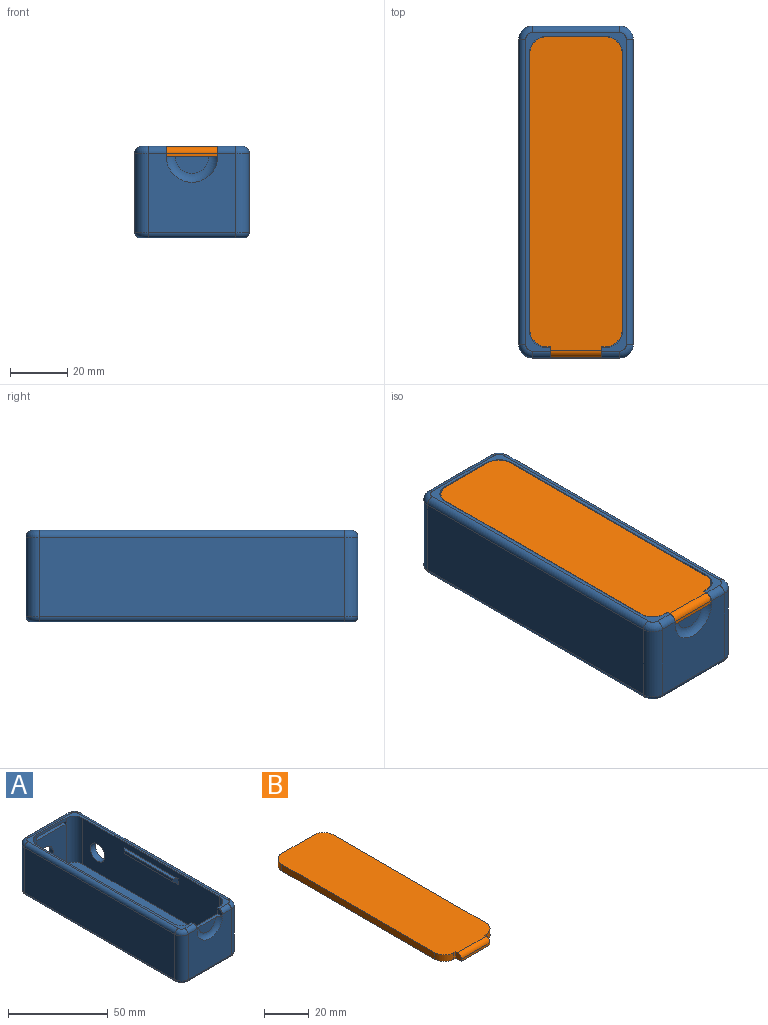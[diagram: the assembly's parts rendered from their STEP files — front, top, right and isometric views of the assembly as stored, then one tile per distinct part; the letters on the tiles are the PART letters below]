
ASSEMBLY  parts=2 mates=1
PART A: 69 faces, bbox 40.8x118.2x32 mm
  f0: plane 96.81x28.4mm, normal (1,0,0), area 2611.4mm2, adj f4,f11,f16,f17,f52,f57,f58,f59
  f1: plane 96.81x28.4mm, normal (-1,0,0), area 2524.9mm2, adj f4,f11,f18,f19,f21,f50,f54,f55
  f2: plane 30.66x27.84mm, normal (0,1,0), area 403.1mm2, adj f12,f13,f34,f44,f47
  f3: plane 20.8x1.7mm, normal (0,-1,0), area 35.4mm2, adj f4,f17,f18,f28
  f4: plane 111.25x35.25mm, normal (0,0,1), area 356.9mm2, adj f0,f1,f3,f5,f16,f17,f18,f19
  f5: plane 28.4x20.8mm, normal (0,1,0), area 526.1mm2, adj f4,f11,f16,f19,f22,f23,f24
  f6: plane 30.64x27.82mm, normal (0,-1,0), area 703.3mm2, adj f14,f15,f22,f24,f30,f38,f41,f61
  f7: plane 24.72x21.87mm, normal (0,-1,0), area 432.7mm2, adj f11,f17,f18,f20,f26,f66
  f8: plane 106.64x27.82mm, normal (1,0,0), area 2880.6mm2, adj f12,f15,f21,f32,f45
  f9: plane 106.64x27.82mm, normal (-1,0,0), area 2967.2mm2, adj f13,f14,f36,f40
  f10: plane 112.4x36.4mm, normal (0,0,-1), area 4084.2mm2, adj f39,f40,f41,f42,f43,f44,f45,f46
  f11: plane 108.8x32.8mm, normal (0,0,1), area 3460.8mm2, adj f0,f1,f5,f7,f16,f17,f18,f19
  f12: cylinder r=4.68mm len=27.82mm, axis (0,0,-1), area 204.5mm2, adj f2,f8,f33,f46
  f13: cylinder r=4.68mm len=27.82mm, axis (0,0,1), area 201.6mm2, adj f2,f9,f35,f42,f47
  f14: cylinder r=4.68mm len=27.82mm, axis (0,0,-1), area 204.5mm2, adj f6,f9,f37,f39
  f15: cylinder r=4.68mm len=27.82mm, axis (0,0,1), area 204.5mm2, adj f6,f8,f31,f43
  f16: cylinder r=6mm len=28.4mm, axis (0,0,1), area 267.6mm2, adj f0,f4,f5,f11
  f17: cylinder r=6mm len=28.4mm, axis (0,0,-1), area 262.1mm2, adj f0,f3,f4,f7,f11,f25,f66
  f18: cylinder r=6mm len=28.4mm, axis (0,0,1), area 267.6mm2, adj f1,f3,f4,f7,f11,f27
  f19: cylinder r=6mm len=28.4mm, axis (0,0,-1), area 267.6mm2, adj f1,f4,f5,f11
  f20: cylinder r=5.25mm len=10.5mm, axis (0,1,0), area 85.8mm2, adj f7,f48
  f21: cylinder r=5.25mm len=10.5mm, axis (1,0,0), area 118.8mm2, adj f1,f8
  f22: plane 3.6x3.6mm, normal (1,0,0), area 11.7mm2, adj f4,f5,f6,f23,f38
  f23: plane 18x3.6mm, normal (0,0,1), area 35.7mm2, adj f5,f22,f24,f60,f61
  f24: plane 3.6x3.6mm, normal (-1,0,0), area 11.7mm2, adj f4,f5,f6,f23,f30
  f25: plane 2.1x2mm, normal (1,0,0), area 4.1mm2, adj f17,f26,f28,f29,f49
  f26: plane 20.8x2.1mm, normal (0,0,1), area 43.7mm2, adj f7,f25,f27,f29
  f27: plane 2.1x2mm, normal (-1,0,0), area 4.1mm2, adj f18,f26,f28,f29,f49
  f28: plane 20.8x1.6mm, normal (0,0,-1), area 33.3mm2, adj f3,f25,f27,f49
  f29: plane 20.8x1.5mm, normal (0,-1,0), area 31.2mm2, adj f25,f26,f27,f49
  f30: cylinder r=2.38mm len=6.32mm, axis (-1,0,0), area 23.6mm2, adj f4,f6,f24,f31
  f31: torus R=2.3mm, axis (0,0,1), area 22.4mm2, adj f4,f15,f30,f32
  f32: cylinder r=2.38mm len=106.64mm, axis (0,-1,0), area 398mm2, adj f4,f8,f31,f33
  f33: torus R=2.3mm, axis (0,0,1), area 22.4mm2, adj f4,f12,f32,f34
  f34: cylinder r=2.38mm len=30.64mm, axis (1,0,0), area 114.4mm2, adj f2,f4,f33,f35
  f35: torus R=2.3mm, axis (0,0,1), area 22.4mm2, adj f4,f13,f34,f36
  f36: cylinder r=2.38mm len=106.64mm, axis (0,1,0), area 398mm2, adj f4,f9,f35,f37
  f37: torus R=2.3mm, axis (0,0,1), area 22.4mm2, adj f4,f14,f36,f38
  f38: cylinder r=2.38mm len=6.32mm, axis (-1,0,0), area 23.6mm2, adj f4,f6,f22,f37
  f39: torus R=2.88mm, axis (0,0,1), area 17.9mm2, adj f10,f14,f40,f41
  f40: cylinder r=1.8mm len=106.64mm, axis (0,-1,0), area 301.5mm2, adj f9,f10,f39,f42
  f41: cylinder r=1.8mm len=30.64mm, axis (1,0,0), area 86.6mm2, adj f6,f10,f39,f43
  f42: torus R=2.88mm, axis (0,0,1), area 17.9mm2, adj f10,f13,f40,f44
  f43: torus R=2.88mm, axis (0,0,1), area 17.9mm2, adj f10,f15,f41,f45
  f44: cylinder r=1.8mm len=30.64mm, axis (-1,0,0), area 86.6mm2, adj f2,f10,f42,f46
  f45: cylinder r=1.8mm len=106.64mm, axis (0,1,0), area 301.5mm2, adj f8,f10,f43,f46
  f46: torus R=2.88mm, axis (0,0,1), area 17.9mm2, adj f10,f12,f44,f45
  f47: cylinder r=12mm len=24mm, axis (0,1,0), area 74.5mm2, adj f2,f13,f48
  f48: plane 24x24mm, normal (0,1,0), area 365.8mm2, adj f20,f47
  f49: cylinder r=0.5mm len=20.8mm, axis (-1,0,0), area 16.3mm2, adj f25,f27,f28,f29
  f50: plane 38.28x1.8mm, normal (0,0,1), area 65.7mm2, adj f1,f51,f54,f56
  f51: plane 34.68x1.8mm, normal (-1,0,0), area 62.4mm2, adj f50,f54,f55,f56
  f52: plane 38.28x1.8mm, normal (0,0,1), area 65.7mm2, adj f0,f53,f57,f59
  f53: plane 34.68x1.8mm, normal (1,0,0), area 62.4mm2, adj f52,f57,f58,f59
  f54: plane 3.6x1.8mm, normal (-0.71,0.71,0), area 6.9mm2, adj f1,f50,f51,f55
  f55: plane 38.28x1.8mm, normal (-0.71,0,-0.71), area 92.9mm2, adj f1,f51,f54,f56
  f56: plane 3.6x1.8mm, normal (-0.71,-0.71,0), area 6.9mm2, adj f1,f50,f51,f55
  f57: plane 3.6x1.8mm, normal (0.71,-0.71,0), area 6.9mm2, adj f0,f52,f53,f58
  f58: plane 38.28x1.8mm, normal (0.71,0,-0.71), area 92.9mm2, adj f0,f53,f57,f59
  f59: plane 3.6x1.8mm, normal (0.71,0.71,0), area 6.9mm2, adj f0,f52,f53,f58
  f60: plane 11.76x5.88mm, normal (0,-1,0), area 54.4mm2, adj f23,f61
  f61: torus R=5.88mm, axis (0,1,0), area 90mm2, adj f6,f23,f60
  f62: cylinder r=1.5mm len=3mm, axis (0,0,-1), area 28.3mm2, adj f63,f68
  f63: plane 3x3mm, normal (0,0,1), area 7.1mm2, adj f62
  f64: cylinder r=1.5mm len=3mm, axis (0,0,-1), area 28.3mm2, adj f65,f67
  f65: plane 3x3mm, normal (0,0,1), area 7.1mm2, adj f64
  f66: cylinder r=7.45mm len=6.96mm, axis (0,1,0), area 0mm2, adj f7,f17
  f67: torus R=3.5mm, axis (0,0,1), area 44mm2, adj f11,f64
  f68: torus R=3.5mm, axis (0,0,1), area 44mm2, adj f11,f62
PART B: 20 faces, bbox 32.3x113.7x3.6 mm
  f0: plane 3.6x1.15mm, normal (0,-1,0), area 4.1mm2, adj f5,f9,f10,f12
  f1: cylinder r=6mm len=6mm, axis (0,0,-1), area 33.9mm2, adj f2,f8,f9,f10,f15
  f2: plane 20.3x1.8mm, normal (0,1,0), area 36.5mm2, adj f1,f3,f9,f14
  f3: cylinder r=6mm len=6mm, axis (0,0,-1), area 33.9mm2, adj f2,f4,f9,f10,f16
  f4: plane 96.31x3.6mm, normal (-1,0,0), area 346.7mm2, adj f3,f5,f9,f10
  f5: cylinder r=6mm len=6mm, axis (0,0,-1), area 33.9mm2, adj f0,f4,f9,f10
  f6: plane 3.6x1.15mm, normal (0,-1,0), area 4.1mm2, adj f7,f9,f10,f11
  f7: cylinder r=6mm len=6mm, axis (0,0,-1), area 33.9mm2, adj f6,f8,f9,f10
  f8: plane 96.31x3.6mm, normal (1,0,0), area 346.7mm2, adj f1,f7,f9,f10
  f9: plane 109.52x32.3mm, normal (0,0,1), area 3489.2mm2, adj f0,f1,f2,f3,f4,f5,f6,f7
  f10: plane 113.7x32.3mm, normal (0,0,-1), area 3568.6mm2, adj f0,f1,f3,f4,f5,f6,f7,f8
  f11: plane 3.6x3.6mm, normal (1,0,0), area 11.7mm2, adj f6,f9,f10,f13,f18
  f12: plane 3.6x3.6mm, normal (-1,0,0), area 11.7mm2, adj f0,f9,f10,f13,f18
  f13: plane 18x1.22mm, normal (0,-1,0), area 22mm2, adj f10,f11,f12,f18
  f14: plane 20.3x1.3mm, normal (0,0,1), area 26.4mm2, adj f2,f15,f16,f19
  f15: plane 1.8x1.8mm, normal (1,0,0), area 3.2mm2, adj f1,f10,f14,f17,f19
  f16: plane 1.8x1.8mm, normal (-1,0,0), area 3.2mm2, adj f3,f10,f14,f17,f19
  f17: plane 20.3x1.3mm, normal (0,1,0), area 26.4mm2, adj f10,f15,f16,f19
  f18: cylinder r=2.38mm len=18mm, axis (-1,0,0), area 67.2mm2, adj f9,f11,f12,f13
  f19: cylinder r=0.5mm len=20.3mm, axis (-1,0,0), area 15.9mm2, adj f14,f15,f16,f17
PLACE A t=(0,-0.05,-28.3)mm
PLACE B at identity
MATE fastened A.f26 <-> B.f10  axis (0,0,1) through (0,56.45,0)mm
